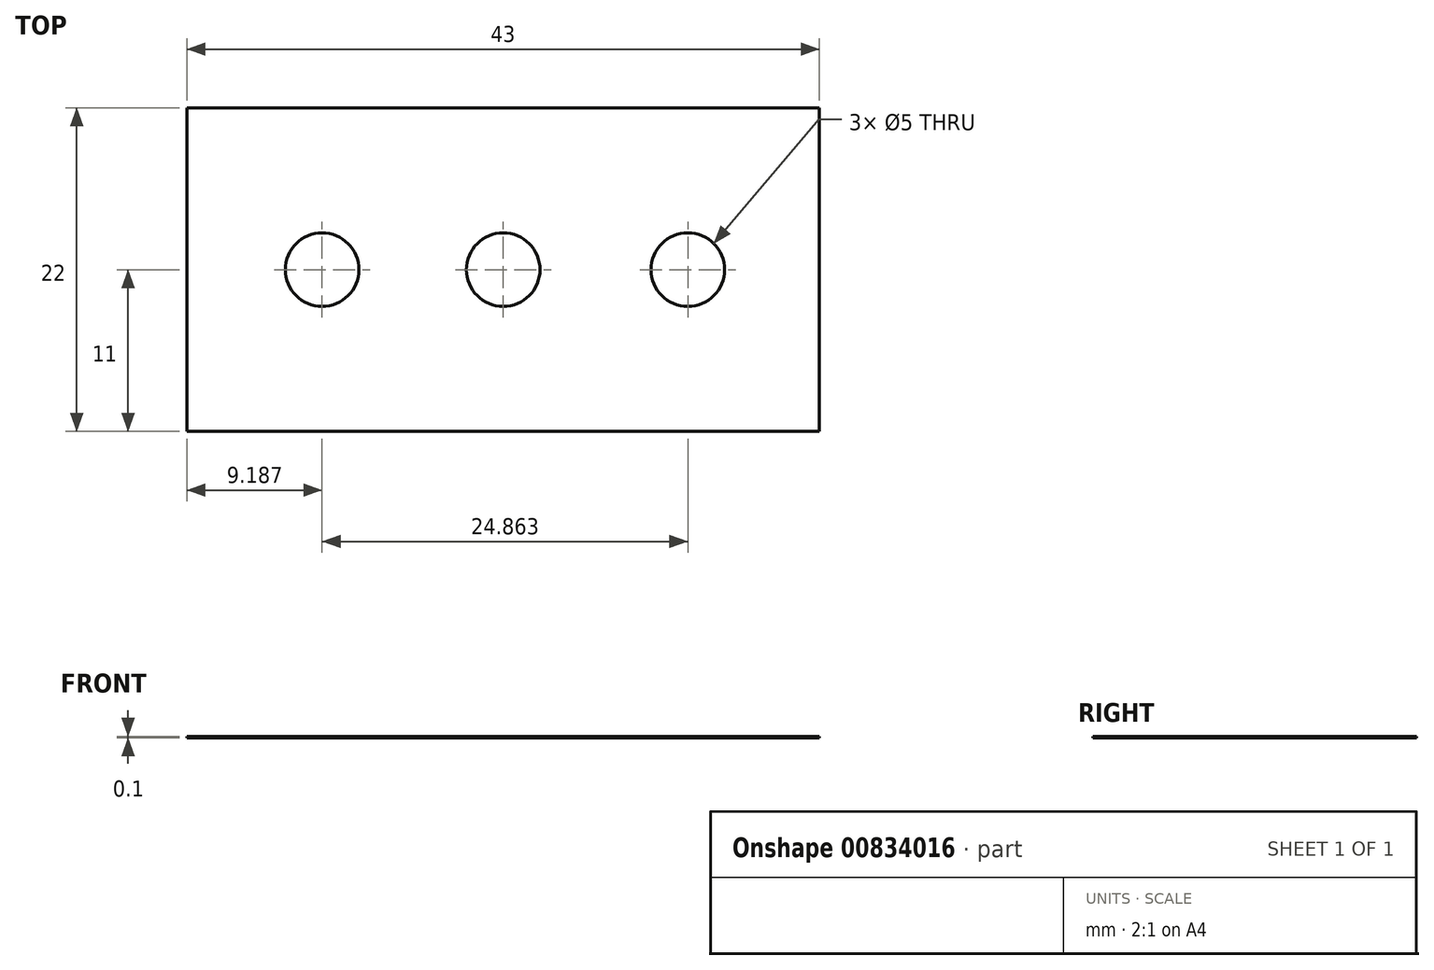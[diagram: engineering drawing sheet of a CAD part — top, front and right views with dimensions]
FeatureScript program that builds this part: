
annotation { "Feature Type Name" : "Feature", "Feature Type Description" : "" }
export const myFeature = defineFeature(function(context is Context, id is Id, definition is map)
    precondition{}
    {
        {
            var Q0;
            Q0=qCreatedBy(makeId("Top.planeOp"),FACE);
            var sketch = newSketch(context, id + "F0", { "sketchPlane" : qUnion([Q0])});
            skLineSegment(sketch, "E0.bottom", {"start": v(21.5, -11) * mm, "end": v(-21.5, -11) * mm});
            skLineSegment(sketch, "E0.top", {"start": v(21.5, 11) * mm, "end": v(-21.5, 11) * mm});
            skLineSegment(sketch, "E0.left", {"start": v(21.5, -11) * mm, "end": v(21.5, 11) * mm});
            skLineSegment(sketch, "E0.right", {"start": v(-21.5, -11) * mm, "end": v(-21.5, 11) * mm});
            skPoint(sketch, "E0.middle", {"position": v(0, 0) * mm});
            skCircle(sketch, "E1", {"center": v(0, 0) * mm, "radius": 2.5 * mm});
            skCircle(sketch, "E2", {"center": v(-12.31, 0) * mm, "radius": 2.5 * mm});
            skCircle(sketch, "E3", {"center": v(12.55, 0) * mm, "radius": 2.5 * mm});
            skSolve(sketch);
        }
        {
            var Q0;
            Q0=makeQuery(id+"F0.imprint","IMPRINT",FACE,{"disambiguationData":[TD([[makeQuery(id+"F0.imprint","IMPRINT",EDGE,{"derivedFrom":sQuery(id+"F0.wireOp",EDGE,"E0.bottom")}),-1.0]])]});
            extrude(context, id + "F1", {"entities" : qUnion([Q0]), "depth" : 0.1 * mm, "offsetDistance" : 25 * mm});
        }
    });
